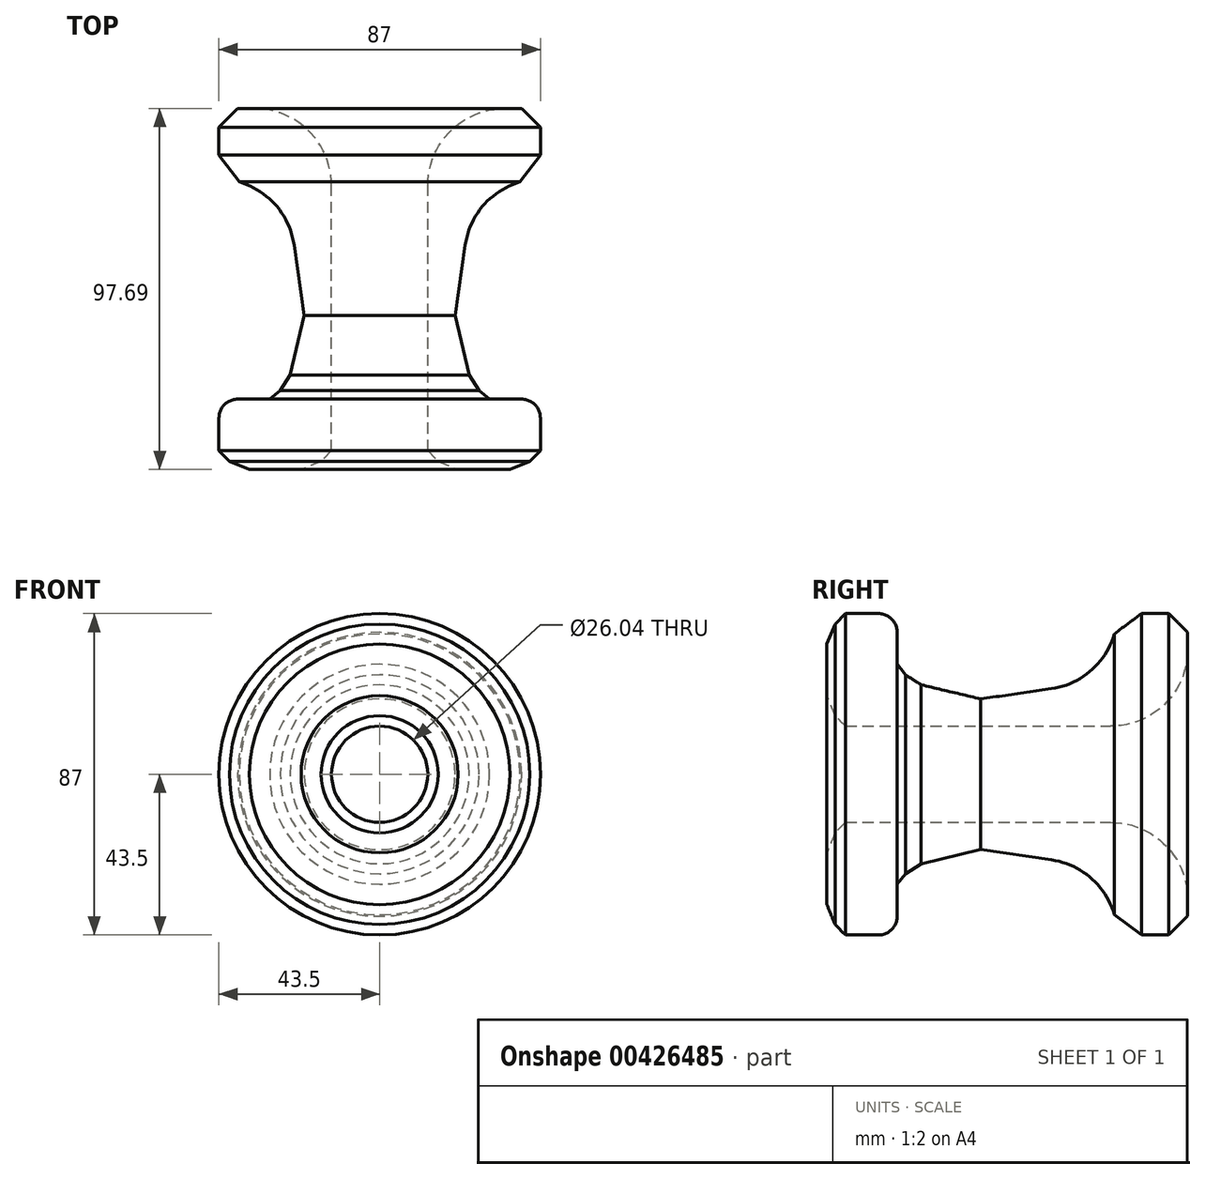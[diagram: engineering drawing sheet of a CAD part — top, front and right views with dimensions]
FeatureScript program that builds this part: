
annotation { "Feature Type Name" : "Feature", "Feature Type Description" : "" }
export const myFeature = defineFeature(function(context is Context, id is Id, definition is map)
    precondition{}
    {
        {
            var Q0;
            Q0=qCreatedBy(makeId("Top.planeOp"),FACE);
            var sketch = newSketch(context, id + "F0", { "sketchPlane" : qUnion([Q0])});
            skLineSegment(sketch, "E0", {"start": v(-13.02, 56.03) * mm, "end": v(-43.5, 56.03) * mm});
            skLineSegment(sketch, "E1", {"start": v(-43.5, 56.03) * mm, "end": v(-43.5, 36.98) * mm});
            skLineSegment(sketch, "E2", {"start": v(-43.5, 36.98) * mm, "end": v(-25.76, 36.98) * mm});
            skLineSegment(sketch, "E3", {"start": v(-25.76, 36.98) * mm, "end": v(-20.4, 0) * mm});
            skLineSegment(sketch, "E4", {"start": v(-20.4, 0) * mm, "end": v(-25.76, -22.61) * mm});
            skLineSegment(sketch, "E5", {"start": v(-25.76, -22.61) * mm, "end": v(-43.5, -22.61) * mm});
            skLineSegment(sketch, "E6", {"start": v(-43.5, -22.61) * mm, "end": v(-43.5, -41.66) * mm});
            skLineSegment(sketch, "E7", {"start": v(-43.5, -41.66) * mm, "end": v(-13.02, -41.66) * mm});
            skLineSegment(sketch, "E8", {"start": v(-13.02, -41.66) * mm, "end": v(-13.02, 56.03) * mm});
            skLineSegment(sketch, "E9", {"start": v(0, 52.45) * mm, "end": v(0, -41.66) * mm, "construction": true});
            skSolve(sketch);
        }
        {
            var Q0;
            Q0=makeQuery(id+"F0.imprint","IMPRINT",FACE,{"disambiguationData":[TD([[makeQuery(id+"F0.imprint","IMPRINT",EDGE,{"derivedFrom":sQuery(id+"F0.wireOp",EDGE,"E0")}),1.0]])]});
            var Q1;
            Q1=sQuery(id+"F0.wireOp",EDGE,"E9");
            revolve(context, id + "F1", {"entities" : qUnion([Q0]), "axis" : qUnion([Q1]), "revolveType" : RevolveType.FULL});
        }
        {
            var Q0;
            Q0=makeQuery(id+"F1.opRevolve","SWEPT_EDGE",EDGE,{"disambiguationData":[OSD([sQuery(id+"F0.wireOp",EDGE,"E0"),sQuery(id+"F0.wireOp",EDGE,"E8")])]});
            var Q1;
            Q1=makeQuery(id+"F1.opRevolve","SWEPT_EDGE",EDGE,{"disambiguationData":[OSD([sQuery(id+"F0.wireOp",EDGE,"E2"),sQuery(id+"F0.wireOp",EDGE,"E3")])]});
            fillet(context, id + "F2", {"entities" : qUnion([Q0, Q1]), "radius" : 20.85 * mm, "tangentPropagation" : true, "allowEdgeOverflow" : false});
        }
        {
            var Q0;
            Q0=makeQuery(id+"F1.opRevolve","SWEPT_EDGE",EDGE,{"disambiguationData":[OSD([sQuery(id+"F0.wireOp",EDGE,"E4"),sQuery(id+"F0.wireOp",EDGE,"E5")])]});
            var Q1;
            Q1=makeQuery(id+"F1.opRevolve","SWEPT_EDGE",EDGE,{"disambiguationData":[OSD([sQuery(id+"F0.wireOp",EDGE,"E7"),sQuery(id+"F0.wireOp",EDGE,"E8")])]});
            var Q2;
            Q2=makeQuery(id+"F1.opRevolve","SWEPT_EDGE",EDGE,{"disambiguationData":[OSD([sQuery(id+"F0.wireOp",EDGE,"E6"),sQuery(id+"F0.wireOp",EDGE,"E7")])]});
            chamfer(context, id + "F3", {"entities" : qUnion([Q0, Q1, Q2]), "width" : 5.08 * mm, "tangentPropagation" : true});
        }
        {
            var Q0;
            Q0=makeQuery(id+"F2.opFillet","BLEND_EDGE",EDGE,{"blendedFrom":[makeQuery(id+"F1.opRevolve","SWEPT_EDGE",EDGE,{"disambiguationData":[OSD([sQuery(id+"F0.wireOp",EDGE,"E2"),sQuery(id+"F0.wireOp",EDGE,"E3")])]}),makeQuery(id+"F1.opRevolve","SWEPT_FACE",FACE,{"disambiguationData":[OSD([sQuery(id+"F0.wireOp",EDGE,"E1")])]})],"blendedInto":[makeQuery(id+"F1.opRevolve","SWEPT_FACE",FACE,{"disambiguationData":[OSD([sQuery(id+"F0.wireOp",EDGE,"E1")])]})]});
            var Q1;
            {var subQ0=sQuery(id+"F0.wireOp",EDGE,"E4");Q1=makeQuery(id+"F3.opChamfer","BLEND_EDGE",EDGE,{"blendedFrom":[makeQuery(id+"F1.opRevolve","SWEPT_EDGE",EDGE,{"disambiguationData":[OSD([subQ0,sQuery(id+"F0.wireOp",EDGE,"E5")])]}),makeQuery(id+"F1.opRevolve","SWEPT_FACE",FACE,{"disambiguationData":[OSD([subQ0])]})],"blendedInto":[makeQuery(id+"F1.opRevolve","SWEPT_FACE",FACE,{"disambiguationData":[OSD([subQ0])]})]});}
            var Q2;
            Q2=makeQuery(id+"F1.opRevolve","SWEPT_FACE",FACE,{"disambiguationData":[OSD([sQuery(id+"F0.wireOp",EDGE,"E7")])]});
            chamfer(context, id + "F4", {"entities" : qUnion([Q0, Q1, Q2]), "width" : 7.62 * mm, "tangentPropagation" : true});
        }
        {
            var Q0;
            Q0=makeQuery(id+"F1.opRevolve","SWEPT_EDGE",EDGE,{"disambiguationData":[OSD([sQuery(id+"F0.wireOp",EDGE,"E5"),sQuery(id+"F0.wireOp",EDGE,"E6")])]});
            fillet(context, id + "F5", {"entities" : qUnion([Q0]), "radius" : 5.08 * mm, "tangentPropagation" : true, "allowEdgeOverflow" : false});
        }
        {
            var Q0;
            Q0=makeQuery(id+"F1.opRevolve","SWEPT_EDGE",EDGE,{"disambiguationData":[OSD([sQuery(id+"F0.wireOp",EDGE,"E0"),sQuery(id+"F0.wireOp",EDGE,"E1")])]});
            chamfer(context, id + "F6", {"entities" : qUnion([Q0]), "width" : 5.08 * mm, "tangentPropagation" : true});
        }
    });
